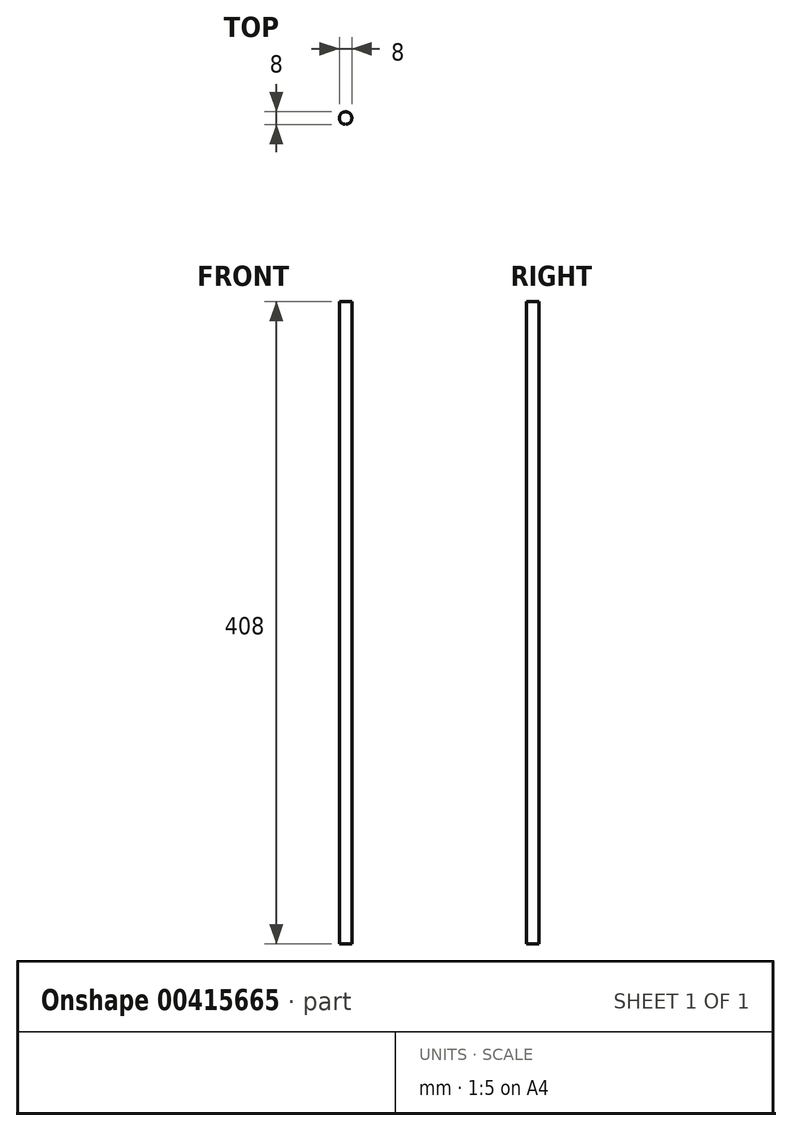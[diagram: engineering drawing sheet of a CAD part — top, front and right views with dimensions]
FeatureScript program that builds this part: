
annotation { "Feature Type Name" : "Feature", "Feature Type Description" : "" }
export const myFeature = defineFeature(function(context is Context, id is Id, definition is map)
    precondition{}
    {
        {
            var Q0;
            Q0=qCreatedBy(makeId("Top.planeOp"),FACE);
            var sketch = newSketch(context, id + "F0", { "sketchPlane" : qUnion([Q0])});
            skCircle(sketch, "E0", {"center": v(0, 0) * mm, "radius": 4 * mm});
            skSolve(sketch);
        }
        {
            var Q0;
            Q0=makeQuery(id+"F0.imprint","IMPRINT",FACE,{"disambiguationData":[TD([[makeQuery(id+"F0.imprint","IMPRINT",EDGE,{"derivedFrom":sQuery(id+"F0.wireOp",EDGE,"E0")}),1.0]])]});
            var Q1;
            Q1=sQuery(id+"F0.wireOp",EDGE,"E0");
            extrude(context, id + "F1", {"entities" : qUnion([Q0]), "surfaceEntities" : qUnion([Q1]), "depth" : 408 * mm});
        }
    });
